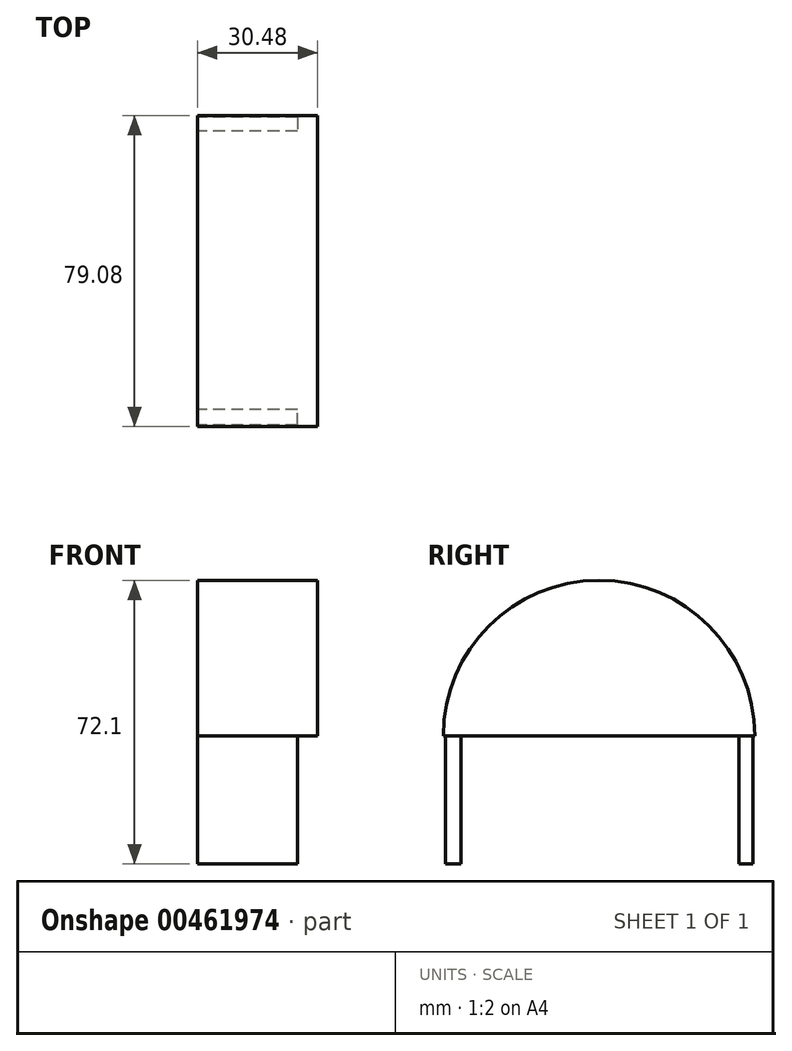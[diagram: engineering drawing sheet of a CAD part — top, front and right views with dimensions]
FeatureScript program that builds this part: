
annotation { "Feature Type Name" : "Feature", "Feature Type Description" : "" }
export const myFeature = defineFeature(function(context is Context, id is Id, definition is map)
    precondition{}
    {
        {
            var Q0;
            Q0=qCreatedBy(makeId("Right.planeOp"),FACE);
            var sketch = newSketch(context, id + "F0", { "sketchPlane" : qUnion([Q0])});
            skArc(sketch, "E0", {"start": v(39.54, 0) * mm, "mid": v(0, 39.54) * mm, "end": v(-39.54, 0) * mm});
            skLineSegment(sketch, "E1", {"start": v(-39.54, 0) * mm, "end": v(39.54, 0) * mm});
            skSolve(sketch);
        }
        {
            var Q0;
            Q0=makeQuery(id+"F0.imprint","IMPRINT",FACE,{"disambiguationData":[TD([[makeQuery(id+"F0.imprint","IMPRINT",EDGE,{"derivedFrom":sQuery(id+"F0.wireOp",EDGE,"E0")}),1.0]])]});
            extrude(context, id + "F1", {"entities" : qUnion([Q0]), "depth" : 5.08 * mm});
        }
        {
            var Q0;
            Q0=makeQuery(id+"F1.opExtrude","CAP_FACE",FACE,{"disambiguationData":[OSD([sQuery(id+"F0.wireOp",EDGE,"E0"),sQuery(id+"F0.wireOp",EDGE,"E1")])],"isStart":false});
            extrude(context, id + "F2", {"entities" : qUnion([Q0]), "operationType" : NewBodyOperationType.ADD, "depth" : 25.4 * mm});
        }
        {
            var Q0;
            Q0=qCreatedBy(makeId("Right.planeOp"),FACE);
            var sketch = newSketch(context, id + "F3", { "sketchPlane" : qUnion([Q0])});
            skLineSegment(sketch, "E2.bottom", {"start": v(39.07, 0) * mm, "end": v(35.59, 0) * mm});
            skLineSegment(sketch, "E2.top", {"start": v(39.07, -32.56) * mm, "end": v(35.59, -32.56) * mm});
            skLineSegment(sketch, "E2.left", {"start": v(39.07, 0) * mm, "end": v(39.07, -32.56) * mm});
            skLineSegment(sketch, "E2.right", {"start": v(35.59, 0) * mm, "end": v(35.59, -32.56) * mm});
            skLineSegment(sketch, "E3.bottom", {"start": v(-39.07, 0) * mm, "end": v(-35.12, 0) * mm});
            skLineSegment(sketch, "E3.top", {"start": v(-39.07, -32.56) * mm, "end": v(-35.12, -32.56) * mm});
            skLineSegment(sketch, "E3.left", {"start": v(-39.07, 0) * mm, "end": v(-39.07, -32.56) * mm});
            skLineSegment(sketch, "E3.right", {"start": v(-35.12, 0) * mm, "end": v(-35.12, -32.56) * mm});
            skLineSegment(sketch, "E4", {"start": v(39.07, -32.56) * mm, "end": v(-41.87, -32.56) * mm});
            skSolve(sketch);
        }
        {
            var Q0;
            Q0=makeQuery(id+"F3.imprint","IMPRINT",FACE,{"disambiguationData":[TD([[makeQuery(id+"F3.imprint","IMPRINT",EDGE,{"derivedFrom":sQuery(id+"F3.wireOp",EDGE,"E2.bottom")}),1.0]])]});
            var Q1;
            Q1=makeQuery(id+"F3.imprint","IMPRINT",FACE,{"disambiguationData":[TD([[makeQuery(id+"F3.imprint","IMPRINT",EDGE,{"derivedFrom":sQuery(id+"F3.wireOp",EDGE,"E3.bottom")}),-1.0]])]});
            extrude(context, id + "F4", {"entities" : qUnion([Q0, Q1]), "operationType" : NewBodyOperationType.ADD, "depth" : 25.4 * mm});
        }
    });
